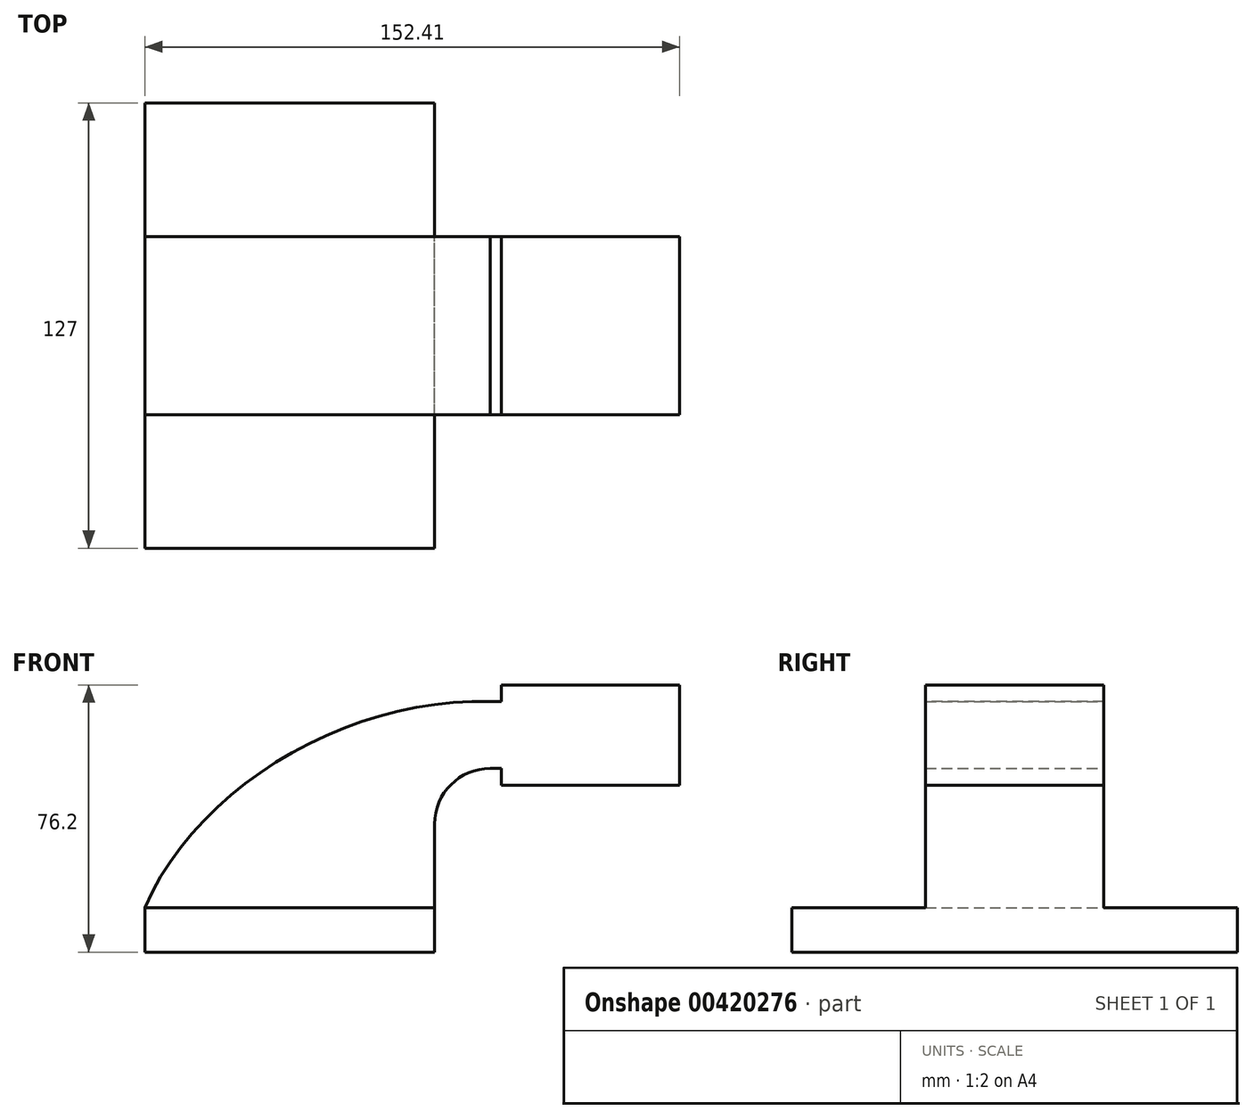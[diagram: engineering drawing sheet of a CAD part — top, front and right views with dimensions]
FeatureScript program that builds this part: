
annotation { "Feature Type Name" : "Feature", "Feature Type Description" : "" }
export const myFeature = defineFeature(function(context is Context, id is Id, definition is map)
    precondition{}
    {
        {
            var Q0;
            Q0=qCreatedBy(makeId("Front.planeOp"),FACE);
            var sketch = newSketch(context, id + "F0", { "sketchPlane" : qUnion([Q0])});
            skLineSegment(sketch, "E0.bottom", {"start": v(-41.28, 6.35) * mm, "end": v(41.28, 6.35) * mm});
            skLineSegment(sketch, "E0.top", {"start": v(-41.28, -6.35) * mm, "end": v(41.28, -6.35) * mm});
            skLineSegment(sketch, "E0.left", {"start": v(-41.28, 6.35) * mm, "end": v(-41.28, -6.35) * mm});
            skLineSegment(sketch, "E0.right", {"start": v(41.28, 6.35) * mm, "end": v(41.28, -6.35) * mm});
            skPoint(sketch, "E0.middle", {"position": v(0, 0) * mm});
            skLineSegment(sketch, "E1.bottom", {"start": v(111.12, 41.27) * mm, "end": v(60.32, 41.27) * mm});
            skLineSegment(sketch, "E1.top", {"start": v(111.12, 69.85) * mm, "end": v(60.32, 69.85) * mm});
            skLineSegment(sketch, "E1.left", {"start": v(111.12, 41.27) * mm, "end": v(111.12, 69.85) * mm});
            skLineSegment(sketch, "E1.right", {"start": v(60.32, 41.27) * mm, "end": v(60.32, 69.85) * mm});
            skPoint(sketch, "E1.middle", {"position": v(85.72, 55.56) * mm});
            skLineSegment(sketch, "E2", {"start": v(41.27, 6.35) * mm, "end": v(41.27, 30.18) * mm});
            skArc(sketch, "E3", {"start": v(41.27, 30.18) * mm, "mid": v(45.92, 41.4) * mm, "end": v(57.15, 46.05) * mm});
            skLineSegment(sketch, "E4", {"start": v(57.15, 46.05) * mm, "end": v(91.45, 46.05) * mm});
            skLineSegment(sketch, "E5.0", {"start": v(57.15, 65.1) * mm, "end": v(91.45, 65.1) * mm});
            skArc(sketch, "E5.1", {"start": v(22.22, 30.18) * mm, "mid": v(32.45, 54.87) * mm, "end": v(57.15, 65.1) * mm});
            skLineSegment(sketch, "E5.2", {"start": v(22.23, 6.35) * mm, "end": v(22.23, 30.18) * mm});
            skLineSegment(sketch, "E6", {"start": v(85.72, 55.56) * mm, "end": v(85.72, 73.5) * mm});
            skPoint(sketch, "E6.endSnap0", {"position": v(85.72, 69.85) * mm});
            skFitSpline(sketch, "E7", {"points": [v(-41.28, 6.35) * mm, v(57.15, 65.1) * mm], "startDerivative": vector(44.42, 103.82) * mm, "endDerivative": vector(121.02, -3.75) * mm});
            skSolve(sketch);
        }
        {
            var Q0;
            Q0=makeQuery(id+"F0.imprint","IMPRINT",FACE,{"disambiguationData":[TD([[makeQuery(id+"F0.imprint","IMPRINT",EDGE,{"derivedFrom":sQuery(id+"F0.wireOp",EDGE,"E0.top")}),1.0]])]});
            extrude(context, id + "F1", {"entities" : qUnion([Q0]), "endBound" : BoundingType.SYMMETRIC, "depth" : 127 * mm});
        }
        {
            var Q0;
            Q0 = qSketchRegion(id + "F0", true);
            extrude(context, id + "F2", {"entities" : qUnion([Q0]), "operationType" : NewBodyOperationType.ADD, "endBound" : BoundingType.SYMMETRIC, "depth" : 50.8 * mm});
        }
    });
